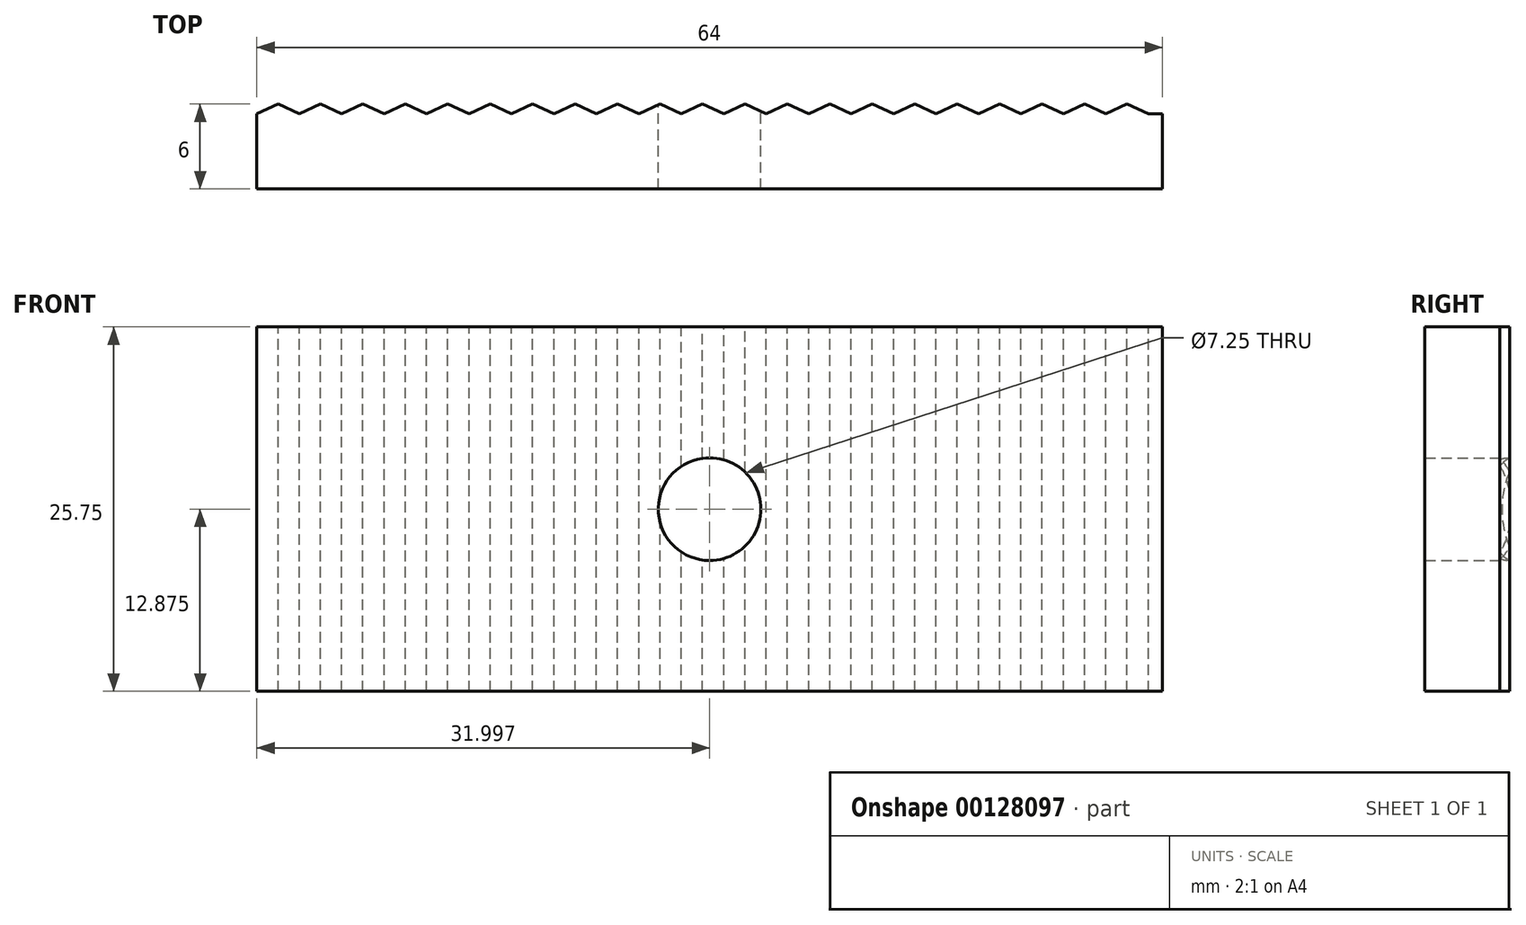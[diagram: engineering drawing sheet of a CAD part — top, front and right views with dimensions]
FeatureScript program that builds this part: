
annotation { "Feature Type Name" : "Feature", "Feature Type Description" : "" }
export const myFeature = defineFeature(function(context is Context, id is Id, definition is map)
    precondition{}
    {
        {
            var Q0;
            Q0=qCreatedBy(makeId("Front.planeOp"),FACE);
            var sketch = newSketch(context, id + "F0", { "sketchPlane" : qUnion([Q0])});
            skLineSegment(sketch, "E0.bottom", {"start": v(-34.42, 25.75) * mm, "end": v(29.58, 25.75) * mm});
            skLineSegment(sketch, "E0.top", {"start": v(-34.42, 0) * mm, "end": v(29.58, 0) * mm});
            skLineSegment(sketch, "E0.left", {"start": v(-34.42, 25.75) * mm, "end": v(-34.42, 0) * mm});
            skLineSegment(sketch, "E0.right", {"start": v(29.58, 25.75) * mm, "end": v(29.58, 0) * mm});
            skCircle(sketch, "E1", {"center": v(-2.42, 12.87) * mm, "radius": 3.62 * mm});
            skSolve(sketch);
        }
        {
            var Q0;
            Q0=makeQuery(id+"F0.imprint","IMPRINT",FACE,{"disambiguationData":[TD([[makeQuery(id+"F0.imprint","IMPRINT",EDGE,{"derivedFrom":sQuery(id+"F0.wireOp",EDGE,"E0.bottom")}),-1.0]])]});
            extrude(context, id + "F1", {"entities" : qUnion([Q0]), "depth" : 6 * mm});
        }
        {
            var Q0;
            Q0=makeQuery(id+"F1.opExtrude","SWEPT_FACE",FACE,{"disambiguationData":[OSD([sQuery(id+"F0.wireOp",EDGE,"E0.bottom")])]});
            var sketch = newSketch(context, id + "F2", { "sketchPlane" : qUnion([Q0])});
            skLineSegment(sketch, "E2.bottom", {"start": v(-34.42, -0.7) * mm, "end": v(29.58, -0.7) * mm});
            skLineSegment(sketch, "E2.top", {"start": v(-34.42, 3.12) * mm, "end": v(29.58, 3.12) * mm});
            skLineSegment(sketch, "E2.left", {"start": v(-34.42, -0.7) * mm, "end": v(-34.42, 3.12) * mm});
            skLineSegment(sketch, "E2.right", {"start": v(29.58, -0.7) * mm, "end": v(29.58, 3.12) * mm});
            skLineSegment(sketch, "E3", {"start": v(-34.42, -0.7) * mm, "end": v(-32.92, 0) * mm});
            skLineSegment(sketch, "E4", {"start": v(-32.92, 0) * mm, "end": v(-31.42, -0.7) * mm});
            skLineSegment(sketch, "E5.1.0.0", {"start": v(-31.42, -0.7) * mm, "end": v(-29.92, 0) * mm});
            skLineSegment(sketch, "E5.1.0.1", {"start": v(-29.92, 0) * mm, "end": v(-28.42, -0.7) * mm});
            skLineSegment(sketch, "E5.2.0.0", {"start": v(-28.42, -0.7) * mm, "end": v(-26.92, 0) * mm});
            skLineSegment(sketch, "E5.2.0.1", {"start": v(-26.92, 0) * mm, "end": v(-25.42, -0.7) * mm});
            skLineSegment(sketch, "E5.3.0.0", {"start": v(-25.42, -0.7) * mm, "end": v(-23.92, 0) * mm});
            skLineSegment(sketch, "E5.3.0.1", {"start": v(-23.92, 0) * mm, "end": v(-22.42, -0.7) * mm});
            skLineSegment(sketch, "E5.4.0.0", {"start": v(-22.42, -0.7) * mm, "end": v(-20.92, 0) * mm});
            skLineSegment(sketch, "E5.4.0.1", {"start": v(-20.92, 0) * mm, "end": v(-19.42, -0.7) * mm});
            skLineSegment(sketch, "E5.5.0.0", {"start": v(-19.42, -0.7) * mm, "end": v(-17.92, 0) * mm});
            skLineSegment(sketch, "E5.5.0.1", {"start": v(-17.92, 0) * mm, "end": v(-16.42, -0.7) * mm});
            skLineSegment(sketch, "E5.6.0.0", {"start": v(-16.42, -0.7) * mm, "end": v(-14.92, 0) * mm});
            skLineSegment(sketch, "E5.6.0.1", {"start": v(-14.92, 0) * mm, "end": v(-13.42, -0.7) * mm});
            skLineSegment(sketch, "E5.7.0.0", {"start": v(-13.42, -0.7) * mm, "end": v(-11.92, 0) * mm});
            skLineSegment(sketch, "E5.7.0.1", {"start": v(-11.92, 0) * mm, "end": v(-10.42, -0.7) * mm});
            skLineSegment(sketch, "E5.8.0.0", {"start": v(-10.42, -0.7) * mm, "end": v(-8.92, 0) * mm});
            skLineSegment(sketch, "E5.8.0.1", {"start": v(-8.92, 0) * mm, "end": v(-7.42, -0.7) * mm});
            skLineSegment(sketch, "E5.9.0.0", {"start": v(-7.42, -0.7) * mm, "end": v(-5.92, 0) * mm});
            skLineSegment(sketch, "E5.9.0.1", {"start": v(-5.92, 0) * mm, "end": v(-4.42, -0.7) * mm});
            skLineSegment(sketch, "E5.10.0.0", {"start": v(-4.42, -0.7) * mm, "end": v(-2.92, 0) * mm});
            skLineSegment(sketch, "E5.10.0.1", {"start": v(-2.92, 0) * mm, "end": v(-1.42, -0.7) * mm});
            skLineSegment(sketch, "E5.11.0.0", {"start": v(-1.42, -0.7) * mm, "end": v(0.08, 0) * mm});
            skLineSegment(sketch, "E5.11.0.1", {"start": v(0.08, 0) * mm, "end": v(1.58, -0.7) * mm});
            skLineSegment(sketch, "E5.12.0.0", {"start": v(1.58, -0.7) * mm, "end": v(3.08, 0) * mm});
            skLineSegment(sketch, "E5.12.0.1", {"start": v(3.08, 0) * mm, "end": v(4.58, -0.7) * mm});
            skLineSegment(sketch, "E5.13.0.0", {"start": v(4.58, -0.7) * mm, "end": v(6.08, 0) * mm});
            skLineSegment(sketch, "E5.13.0.1", {"start": v(6.08, 0) * mm, "end": v(7.58, -0.7) * mm});
            skLineSegment(sketch, "E5.14.0.0", {"start": v(7.58, -0.7) * mm, "end": v(9.08, 0) * mm});
            skLineSegment(sketch, "E5.14.0.1", {"start": v(9.08, 0) * mm, "end": v(10.58, -0.7) * mm});
            skLineSegment(sketch, "E5.15.0.0", {"start": v(10.58, -0.7) * mm, "end": v(12.08, 0) * mm});
            skLineSegment(sketch, "E5.15.0.1", {"start": v(12.08, 0) * mm, "end": v(13.58, -0.7) * mm});
            skLineSegment(sketch, "E5.16.0.0", {"start": v(13.58, -0.7) * mm, "end": v(15.08, 0) * mm});
            skLineSegment(sketch, "E5.16.0.1", {"start": v(15.08, 0) * mm, "end": v(16.58, -0.7) * mm});
            skLineSegment(sketch, "E5.17.0.0", {"start": v(16.58, -0.7) * mm, "end": v(18.08, 0) * mm});
            skLineSegment(sketch, "E5.17.0.1", {"start": v(18.08, 0) * mm, "end": v(19.58, -0.7) * mm});
            skLineSegment(sketch, "E5.18.0.0", {"start": v(19.58, -0.7) * mm, "end": v(21.08, 0) * mm});
            skLineSegment(sketch, "E5.18.0.1", {"start": v(21.08, 0) * mm, "end": v(22.58, -0.7) * mm});
            skLineSegment(sketch, "E5.19.0.0", {"start": v(22.58, -0.7) * mm, "end": v(24.08, 0) * mm});
            skLineSegment(sketch, "E5.19.0.1", {"start": v(24.08, 0) * mm, "end": v(25.58, -0.7) * mm});
            skLineSegment(sketch, "E5.20.0.0", {"start": v(25.58, -0.7) * mm, "end": v(27.08, 0) * mm});
            skLineSegment(sketch, "E5.20.0.1", {"start": v(27.08, 0) * mm, "end": v(28.58, -0.7) * mm});
            skLineSegment(sketch, "E5.direction1", {"start": v(-34.42, -0.7) * mm, "end": v(-31.42, -0.7) * mm, "construction": true});
            skSolve(sketch);
        }
        {
            var Q0;
            {var subQ4=sQuery(id+"F2.wireOp",EDGE,"E3");Q0=makeQuery(id+"F2.imprint","IMPRINT",FACE,{"disambiguationData":[TD([[makeQuery(id+"F2.imprint","IMPRINT",EDGE,{"derivedFrom":subQ4}),1.0]])]});}
            var Q1;
            {var subQ0=sQuery(id+"F2.wireOp",EDGE,"E4");Q1=makeQuery(id+"F2.imprint","IMPRINT",FACE,{"disambiguationData":[TD([[makeQuery(id+"F2.imprint","IMPRINT",EDGE,{"derivedFrom":subQ0}),1.0]])]});}
            var Q2;
            {var subQ0=sQuery(id+"F2.wireOp",EDGE,"E5.1.0.1");Q2=makeQuery(id+"F2.imprint","IMPRINT",FACE,{"disambiguationData":[TD([[makeQuery(id+"F2.imprint","IMPRINT",EDGE,{"derivedFrom":subQ0}),1.0]])]});}
            var Q3;
            {var subQ0=sQuery(id+"F2.wireOp",EDGE,"E5.2.0.1");Q3=makeQuery(id+"F2.imprint","IMPRINT",FACE,{"disambiguationData":[TD([[makeQuery(id+"F2.imprint","IMPRINT",EDGE,{"derivedFrom":subQ0}),1.0]])]});}
            var Q4;
            {var subQ0=sQuery(id+"F2.wireOp",EDGE,"E5.3.0.1");Q4=makeQuery(id+"F2.imprint","IMPRINT",FACE,{"disambiguationData":[TD([[makeQuery(id+"F2.imprint","IMPRINT",EDGE,{"derivedFrom":subQ0}),1.0]])]});}
            var Q5;
            {var subQ0=sQuery(id+"F2.wireOp",EDGE,"E5.4.0.1");Q5=makeQuery(id+"F2.imprint","IMPRINT",FACE,{"disambiguationData":[TD([[makeQuery(id+"F2.imprint","IMPRINT",EDGE,{"derivedFrom":subQ0}),1.0]])]});}
            var Q6;
            {var subQ0=sQuery(id+"F2.wireOp",EDGE,"E5.5.0.1");Q6=makeQuery(id+"F2.imprint","IMPRINT",FACE,{"disambiguationData":[TD([[makeQuery(id+"F2.imprint","IMPRINT",EDGE,{"derivedFrom":subQ0}),1.0]])]});}
            var Q7;
            {var subQ0=sQuery(id+"F2.wireOp",EDGE,"E5.6.0.1");Q7=makeQuery(id+"F2.imprint","IMPRINT",FACE,{"disambiguationData":[TD([[makeQuery(id+"F2.imprint","IMPRINT",EDGE,{"derivedFrom":subQ0}),1.0]])]});}
            var Q8;
            {var subQ0=sQuery(id+"F2.wireOp",EDGE,"E5.7.0.1");Q8=makeQuery(id+"F2.imprint","IMPRINT",FACE,{"disambiguationData":[TD([[makeQuery(id+"F2.imprint","IMPRINT",EDGE,{"derivedFrom":subQ0}),1.0]])]});}
            var Q9;
            {var subQ0=sQuery(id+"F2.wireOp",EDGE,"E5.8.0.1");Q9=makeQuery(id+"F2.imprint","IMPRINT",FACE,{"disambiguationData":[TD([[makeQuery(id+"F2.imprint","IMPRINT",EDGE,{"derivedFrom":subQ0}),1.0]])]});}
            var Q10;
            {var subQ0=sQuery(id+"F2.wireOp",EDGE,"E5.9.0.1");Q10=makeQuery(id+"F2.imprint","IMPRINT",FACE,{"disambiguationData":[TD([[makeQuery(id+"F2.imprint","IMPRINT",EDGE,{"derivedFrom":subQ0}),1.0]])]});}
            var Q11;
            {var subQ0=sQuery(id+"F2.wireOp",EDGE,"E5.10.0.1");Q11=makeQuery(id+"F2.imprint","IMPRINT",FACE,{"disambiguationData":[TD([[makeQuery(id+"F2.imprint","IMPRINT",EDGE,{"derivedFrom":subQ0}),1.0]])]});}
            var Q12;
            {var subQ0=sQuery(id+"F2.wireOp",EDGE,"E5.11.0.1");Q12=makeQuery(id+"F2.imprint","IMPRINT",FACE,{"disambiguationData":[TD([[makeQuery(id+"F2.imprint","IMPRINT",EDGE,{"derivedFrom":subQ0}),1.0]])]});}
            var Q13;
            {var subQ0=sQuery(id+"F2.wireOp",EDGE,"E5.12.0.1");Q13=makeQuery(id+"F2.imprint","IMPRINT",FACE,{"disambiguationData":[TD([[makeQuery(id+"F2.imprint","IMPRINT",EDGE,{"derivedFrom":subQ0}),1.0]])]});}
            var Q14;
            {var subQ0=sQuery(id+"F2.wireOp",EDGE,"E5.13.0.1");Q14=makeQuery(id+"F2.imprint","IMPRINT",FACE,{"disambiguationData":[TD([[makeQuery(id+"F2.imprint","IMPRINT",EDGE,{"derivedFrom":subQ0}),1.0]])]});}
            var Q15;
            {var subQ0=sQuery(id+"F2.wireOp",EDGE,"E5.14.0.1");Q15=makeQuery(id+"F2.imprint","IMPRINT",FACE,{"disambiguationData":[TD([[makeQuery(id+"F2.imprint","IMPRINT",EDGE,{"derivedFrom":subQ0}),1.0]])]});}
            var Q16;
            {var subQ0=sQuery(id+"F2.wireOp",EDGE,"E5.15.0.1");Q16=makeQuery(id+"F2.imprint","IMPRINT",FACE,{"disambiguationData":[TD([[makeQuery(id+"F2.imprint","IMPRINT",EDGE,{"derivedFrom":subQ0}),1.0]])]});}
            var Q17;
            {var subQ0=sQuery(id+"F2.wireOp",EDGE,"E5.16.0.1");Q17=makeQuery(id+"F2.imprint","IMPRINT",FACE,{"disambiguationData":[TD([[makeQuery(id+"F2.imprint","IMPRINT",EDGE,{"derivedFrom":subQ0}),1.0]])]});}
            var Q18;
            {var subQ0=sQuery(id+"F2.wireOp",EDGE,"E5.17.0.1");Q18=makeQuery(id+"F2.imprint","IMPRINT",FACE,{"disambiguationData":[TD([[makeQuery(id+"F2.imprint","IMPRINT",EDGE,{"derivedFrom":subQ0}),1.0]])]});}
            var Q19;
            {var subQ0=sQuery(id+"F2.wireOp",EDGE,"E5.18.0.1");Q19=makeQuery(id+"F2.imprint","IMPRINT",FACE,{"disambiguationData":[TD([[makeQuery(id+"F2.imprint","IMPRINT",EDGE,{"derivedFrom":subQ0}),1.0]])]});}
            var Q20;
            {var subQ0=sQuery(id+"F2.wireOp",EDGE,"E5.19.0.1");Q20=makeQuery(id+"F2.imprint","IMPRINT",FACE,{"disambiguationData":[TD([[makeQuery(id+"F2.imprint","IMPRINT",EDGE,{"derivedFrom":subQ0}),1.0]])]});}
            var Q21;
            {var subQ4=sQuery(id+"F2.wireOp",EDGE,"E5.20.0.1");Q21=makeQuery(id+"F2.imprint","IMPRINT",FACE,{"disambiguationData":[TD([[makeQuery(id+"F2.imprint","IMPRINT",EDGE,{"derivedFrom":subQ4}),1.0]])]});}
            extrude(context, id + "F3", {"entities" : qUnion([Q0, Q1, Q2, Q3, Q4, Q5, Q6, Q7, Q8, Q9, Q10, Q11, Q12, Q13, Q14, Q15, Q16, Q17, Q18, Q19, Q20, Q21]), "operationType" : NewBodyOperationType.REMOVE, "oppositeDirection" : true, "depth" : 26.5 * mm});
        }
    });
